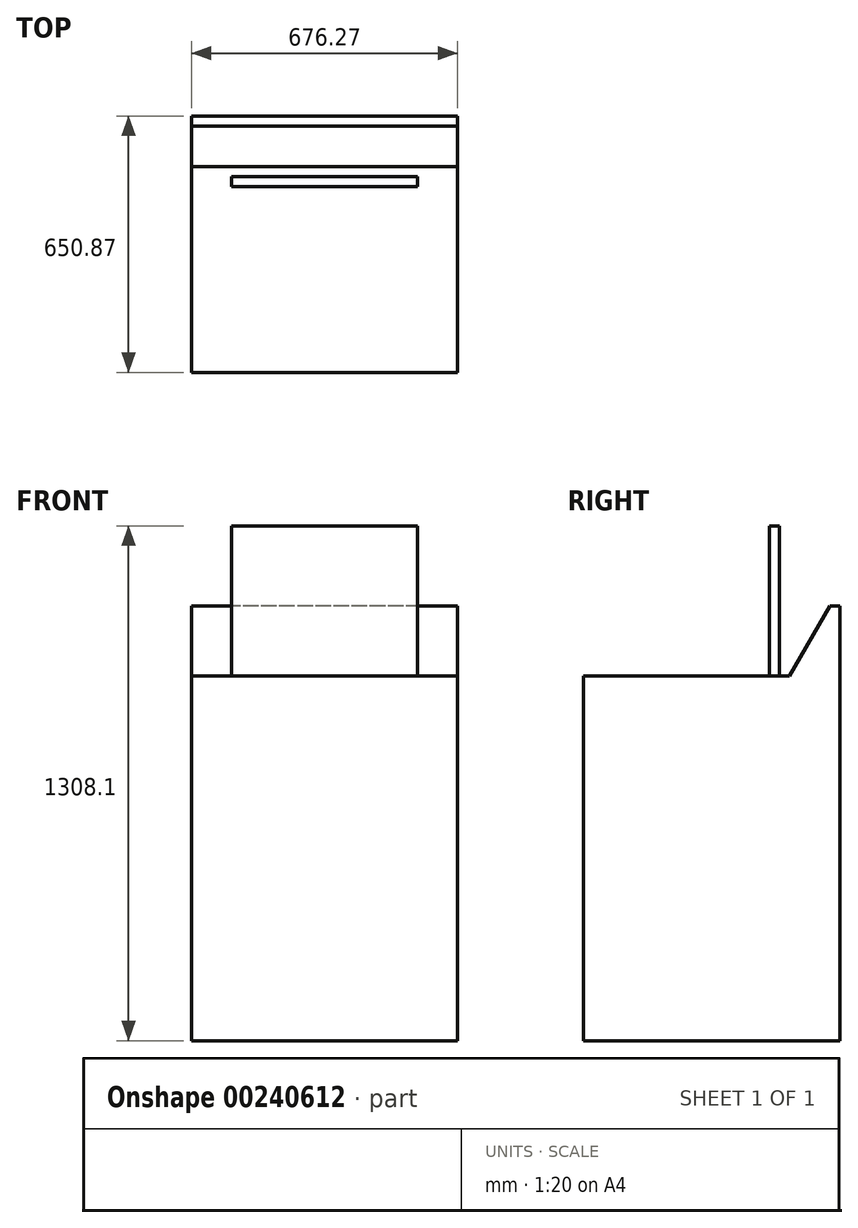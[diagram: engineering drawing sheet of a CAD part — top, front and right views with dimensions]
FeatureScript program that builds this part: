
annotation { "Feature Type Name" : "Feature", "Feature Type Description" : "" }
export const myFeature = defineFeature(function(context is Context, id is Id, definition is map)
    precondition{}
    {
        {
            var Q0;
            Q0=qCreatedBy(makeId("Top.planeOp"),FACE);
            var sketch = newSketch(context, id + "F0", { "sketchPlane" : qUnion([Q0])});
            skLineSegment(sketch, "E0.bottom", {"start": v(-335.8, 397.7) * mm, "end": v(340.47, 397.7) * mm});
            skLineSegment(sketch, "E0.top", {"start": v(-335.8, -253.17) * mm, "end": v(340.47, -253.17) * mm});
            skLineSegment(sketch, "E0.left", {"start": v(-335.8, 397.7) * mm, "end": v(-335.8, -253.17) * mm});
            skLineSegment(sketch, "E0.right", {"start": v(340.47, 397.7) * mm, "end": v(340.47, -253.17) * mm});
            skSolve(sketch);
        }
        {
            var Q0;
            Q0=makeQuery(id+"F0.imprint","IMPRINT",FACE,{"disambiguationData":[TD([[makeQuery(id+"F0.imprint","IMPRINT",EDGE,{"derivedFrom":sQuery(id+"F0.wireOp",EDGE,"E0.bottom")}),-1.0]])]});
            extrude(context, id + "F1", {"entities" : qUnion([Q0]), "depth" : 927.1 * mm, "offsetDistance" : 25.4 * mm});
        }
        {
            var Q0;
            Q0=makeQuery(id+"F1.opExtrude","SWEPT_FACE",FACE,{"disambiguationData":[OSD([sQuery(id+"F0.wireOp",EDGE,"E0.left")])]});
            var sketch = newSketch(context, id + "F2", { "sketchPlane" : qUnion([Q0])});
            skLineSegment(sketch, "E1", {"start": v(-397.7, 927.1) * mm, "end": v(-397.7, 1104.9) * mm});
            skLineSegment(sketch, "E2", {"start": v(-397.7, 1104.9) * mm, "end": v(-372.3, 1104.9) * mm});
            skLineSegment(sketch, "E3", {"start": v(-372.3, 1104.9) * mm, "end": v(-269.65, 927.1) * mm});
            skLineSegment(sketch, "E4", {"start": v(-269.65, 927.1) * mm, "end": v(-397.7, 927.1) * mm});
            skSolve(sketch);
        }
        {
            var Q0;
            Q0=makeQuery(id+"F2.imprint","IMPRINT",FACE,{"disambiguationData":[TD([[makeQuery(id+"F2.imprint","IMPRINT",EDGE,{"derivedFrom":sQuery(id+"F2.wireOp",EDGE,"E1")}),-1.0]])]});
            var Q1;
            Q1=makeQuery(id+"F1.opExtrude","SWEPT_FACE",FACE,{"disambiguationData":[OSD([sQuery(id+"F0.wireOp",EDGE,"E0.right")])]});
            extrude(context, id + "F3", {"entities" : qUnion([Q0]), "operationType" : NewBodyOperationType.ADD, "endBound" : BoundingType.UP_TO_SURFACE, "oppositeDirection" : true, "depth" : 256.54 * mm, "endBoundEntityFace" : qUnion([Q1]), "offsetDistance" : 25.4 * mm});
        }
        {
            var Q0;
            Q0=makeQuery(id+"F1.opExtrude","CAP_FACE",FACE,{"disambiguationData":[OSD([sQuery(id+"F0.wireOp",EDGE,"E0.bottom"),sQuery(id+"F0.wireOp",EDGE,"E0.top"),sQuery(id+"F0.wireOp",EDGE,"E0.left"),sQuery(id+"F0.wireOp",EDGE,"E0.right")])],"isStart":false});
            var sketch = newSketch(context, id + "F4", { "sketchPlane" : qUnion([Q0])});
            skLineSegment(sketch, "E5.bottom", {"start": v(-234.2, 244.25) * mm, "end": v(238.87, 244.25) * mm});
            skLineSegment(sketch, "E5.top", {"start": v(-234.2, 218.85) * mm, "end": v(238.87, 218.85) * mm});
            skLineSegment(sketch, "E5.left", {"start": v(-234.2, 244.25) * mm, "end": v(-234.2, 218.85) * mm});
            skLineSegment(sketch, "E5.right", {"start": v(238.87, 244.25) * mm, "end": v(238.87, 218.85) * mm});
            skSolve(sketch);
        }
        {
            var Q0;
            Q0=makeQuery(id+"F4.imprint","IMPRINT",FACE,{"disambiguationData":[TD([[makeQuery(id+"F4.imprint","IMPRINT",EDGE,{"derivedFrom":sQuery(id+"F4.wireOp",EDGE,"E5.bottom")}),-1.0]])]});
            extrude(context, id + "F5", {"entities" : qUnion([Q0]), "operationType" : NewBodyOperationType.ADD, "depth" : 381 * mm, "offsetDistance" : 25.4 * mm});
        }
    });
